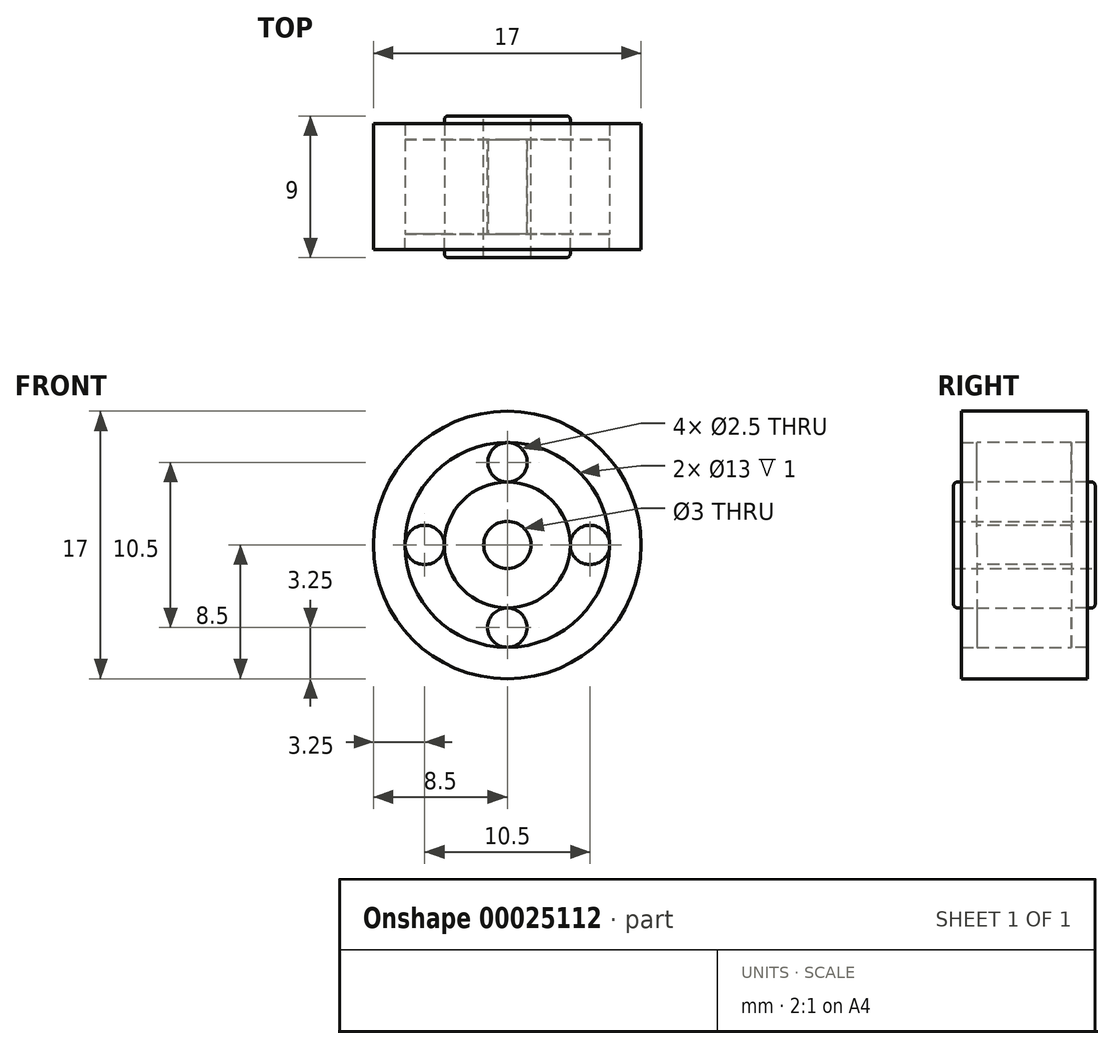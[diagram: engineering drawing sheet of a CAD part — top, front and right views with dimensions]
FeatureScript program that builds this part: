
annotation { "Feature Type Name" : "Feature", "Feature Type Description" : "" }
export const myFeature = defineFeature(function(context is Context, id is Id, definition is map)
    precondition{}
    {
        {
            var Q0;
            Q0=qCreatedBy(makeId("Front.planeOp"),FACE);
            var sketch = newSketch(context, id + "F0", { "sketchPlane" : qUnion([Q0])});
            skCircle(sketch, "E0", {"center": v(0, 0) * mm, "radius": 8.5 * mm});
            skCircle(sketch, "E1", {"center": v(0, 0) * mm, "radius": 1.5 * mm});
            skCircle(sketch, "E2", {"center": v(0, 0) * mm, "radius": 4 * mm});
            skCircle(sketch, "E3", {"center": v(0, 0) * mm, "radius": 6.5 * mm});
            skCircle(sketch, "E4", {"center": v(0, -5.25) * mm, "radius": 1.25 * mm});
            skSolve(sketch);
        }
        {
            var Q0;
            Q0 = qSketchRegion(id + "F0", true);
            var Q1;
            {var subQ3=sQuery(id+"F0.wireOp",EDGE,"E2");Q1=makeQuery(id+"F0.imprint","IMPRINT",FACE,{"disambiguationData":[TD([[makeQuery(id+"F0.imprint","IMPRINT",EDGE,{"derivedFrom":subQ3}),-1.0]])]});}
            var Q2;
            Q2=makeQuery(id+"F0.imprint","IMPRINT",FACE,{"disambiguationData":[TD([[makeQuery(id+"F0.imprint","IMPRINT",EDGE,{"derivedFrom":sQuery(id+"F0.wireOp",EDGE,"E1")}),-1.0]])]});
            extrude(context, id + "F1", {"entities" : qUnion([Q0, Q1, Q2]), "depth" : 6 * mm});
        }
        {
            var Q0;
            Q0=makeQuery(id+"F1.opExtrude","CAP_FACE",FACE,{"disambiguationData":[OSD([sQuery(id+"F0.wireOp",EDGE,"E0"),sQuery(id+"F0.wireOp",EDGE,"E1"),sQuery(id+"F0.wireOp",EDGE,"E4")])],"isStart":false});
            var sketch = newSketch(context, id + "F2", { "sketchPlane" : qUnion([Q0])});
            skCircle(sketch, "E5", {"center": v(0, 0) * mm, "radius": 4 * mm});
            skSolve(sketch);
        }
        {
            var Q0;
            Q0=makeQuery(id+"F2.imprint","IMPRINT",FACE,{"disambiguationData":[TD([[makeQuery(id+"F2.imprint","IMPRINT",EDGE,{"derivedFrom":sQuery(id+"F2.wireOp",EDGE,"E5")}),1.0]])]});
            extrude(context, id + "F3", {"entities" : qUnion([Q0]), "operationType" : NewBodyOperationType.ADD, "depth" : 1.5 * mm});
        }
        {
            var Q0;
            Q0=makeQuery(id+"F1.opExtrude","CAP_FACE",FACE,{"disambiguationData":[OSD([sQuery(id+"F0.wireOp",EDGE,"E0"),sQuery(id+"F0.wireOp",EDGE,"E1"),sQuery(id+"F0.wireOp",EDGE,"E4")])],"isStart":false});
            var sketch = newSketch(context, id + "F4", { "sketchPlane" : qUnion([Q0])});
            skCircle(sketch, "E6", {"center": v(0, 0) * mm, "radius": 6.5 * mm});
            skSolve(sketch);
        }
        {
            var Q0;
            Q0=makeQuery(id+"F4.imprint","IMPRINT",FACE,{"disambiguationData":[TD([[makeQuery(id+"F4.imprint","IMPRINT",EDGE,{"derivedFrom":sQuery(id+"F4.wireOp",EDGE,"E6")}),-1.0]])]});
            extrude(context, id + "F5", {"entities" : qUnion([Q0]), "operationType" : NewBodyOperationType.ADD, "depth" : 1 * mm});
        }
        {
            var Q0;
            Q0=makeQuery(id+"F1.opExtrude","CAP_FACE",FACE,{"disambiguationData":[OSD([sQuery(id+"F0.wireOp",EDGE,"E0"),sQuery(id+"F0.wireOp",EDGE,"E1"),sQuery(id+"F0.wireOp",EDGE,"E4")])],"isStart":false});
            var sketch = newSketch(context, id + "F6", { "sketchPlane" : qUnion([Q0])});
            skLineSegment(sketch, "E7", {"start": v(0, 0) * mm, "end": v(0, -6.5) * mm, "construction": true});
            skLineSegment(sketch, "E8", {"start": v(0, 0) * mm, "end": v(0, 6.5) * mm, "construction": true});
            skLineSegment(sketch, "E9", {"start": v(0, 0) * mm, "end": v(6.5, 0) * mm, "construction": true});
            skLineSegment(sketch, "E10", {"start": v(0, 0) * mm, "end": v(-6.5, 0) * mm, "construction": true});
            skCircle(sketch, "E11", {"center": v(5.25, 0) * mm, "radius": 1.25 * mm});
            skCircle(sketch, "E12", {"center": v(0.01, 5.25) * mm, "radius": 1.25 * mm});
            skCircle(sketch, "E13", {"center": v(-5.25, 0) * mm, "radius": 1.25 * mm});
            skSolve(sketch);
        }
        {
            var Q0;
            {var subQ0=sQuery(id+"F6.wireOp",EDGE,"E11");var subQ2=makeQuery(id+"F6.imprint","INTERSECT",VERTEX,{"derivedFrom":[makeQuery(id+"F5.opExtrude","CAP_EDGE",EDGE,{"disambiguationData":[OSD([sQuery(id+"F4.wireOp",EDGE,"E6")])],"isStart":true}),subQ0]});Q0=makeQuery(id+"F6.imprint","IMPRINT",FACE,{"disambiguationData":[TD([[makeQuery(id+"F6.imprint","IMPRINT",EDGE,{"disambiguationData":[TD([[subQ2,-1.0]])],"derivedFrom":subQ0}),1.0]])]});}
            var Q1;
            {var subQ0=sQuery(id+"F6.wireOp",EDGE,"E13");var subQ2=makeQuery(id+"F6.imprint","INTERSECT",VERTEX,{"derivedFrom":[makeQuery(id+"F5.opExtrude","CAP_EDGE",EDGE,{"disambiguationData":[OSD([sQuery(id+"F4.wireOp",EDGE,"E6")])],"isStart":true}),subQ0]});Q1=makeQuery(id+"F6.imprint","IMPRINT",FACE,{"disambiguationData":[TD([[makeQuery(id+"F6.imprint","IMPRINT",EDGE,{"disambiguationData":[TD([[subQ2,1.0]])],"derivedFrom":subQ0}),1.0]])]});}
            var Q2;
            {var subQ0=sQuery(id+"F6.wireOp",EDGE,"E12");var subQ2=makeQuery(id+"F6.imprint","INTERSECT",VERTEX,{"derivedFrom":[makeQuery(id+"F5.opExtrude","CAP_EDGE",EDGE,{"disambiguationData":[OSD([sQuery(id+"F4.wireOp",EDGE,"E6")])],"isStart":true}),subQ0]});Q2=makeQuery(id+"F6.imprint","IMPRINT",FACE,{"disambiguationData":[TD([[makeQuery(id+"F6.imprint","IMPRINT",EDGE,{"disambiguationData":[TD([[subQ2,-1.0]])],"derivedFrom":subQ0}),1.0]])]});}
            extrude(context, id + "F7", {"entities" : qUnion([Q0, Q1, Q2]), "operationType" : NewBodyOperationType.REMOVE, "oppositeDirection" : true, "depth" : 25.4 * mm});
        }
        {
            var Q0;
            Q0=makeQuery(id+"F1.opExtrude","CAP_FACE",FACE,{"disambiguationData":[OSD([sQuery(id+"F0.wireOp",EDGE,"E0"),sQuery(id+"F0.wireOp",EDGE,"E1"),sQuery(id+"F0.wireOp",EDGE,"E4")])],"isStart":true});
            var sketch = newSketch(context, id + "F8", { "sketchPlane" : qUnion([Q0])});
            skCircle(sketch, "E14", {"center": v(0, 0) * mm, "radius": 4 * mm});
            skSolve(sketch);
        }
        {
            var Q0;
            {var subQ3=sQuery(id+"F0.wireOp",EDGE,"E1");Q0=makeQuery(id+"F8.imprint","IMPRINT",FACE,{"disambiguationData":[TD([[makeQuery(id+"F8.imprint","IMPRINT",EDGE,{"derivedFrom":makeQuery(id+"F1.opExtrude","CAP_EDGE",EDGE,{"disambiguationData":[OSD([subQ3])],"isStart":true})}),1.0]])]});}
            extrude(context, id + "F9", {"entities" : qUnion([Q0]), "operationType" : NewBodyOperationType.ADD, "depth" : 1.5 * mm});
        }
        {
            var Q0;
            Q0=makeQuery(id+"F1.opExtrude","CAP_FACE",FACE,{"disambiguationData":[OSD([sQuery(id+"F0.wireOp",EDGE,"E0"),sQuery(id+"F0.wireOp",EDGE,"E1"),sQuery(id+"F0.wireOp",EDGE,"E4")])],"isStart":true});
            var sketch = newSketch(context, id + "F10", { "sketchPlane" : qUnion([Q0])});
            skCircle(sketch, "E15", {"center": v(0, 0) * mm, "radius": 6.5 * mm});
            skSolve(sketch);
        }
        {
            var Q0;
            {var subQ0=sQuery(id+"F0.wireOp",EDGE,"E0");Q0=makeQuery(id+"F10.imprint","IMPRINT",FACE,{"disambiguationData":[TD([[makeQuery(id+"F10.imprint","IMPRINT",EDGE,{"derivedFrom":makeQuery(id+"F1.opExtrude","CAP_EDGE",EDGE,{"disambiguationData":[OSD([subQ0])],"isStart":true})}),-1.0]])]});}
            extrude(context, id + "F11", {"entities" : qUnion([Q0]), "operationType" : NewBodyOperationType.ADD, "depth" : 1 * mm});
        }
        {
            var Q0;
            Q0=makeQuery(id+"F9.opExtrude","CAP_EDGE",EDGE,{"disambiguationData":[OSD([sQuery(id+"F8.wireOp",EDGE,"E14")])],"isStart":false});
            fillet(context, id + "F12", {"entities" : qUnion([Q0]), "radius" : 0.24 * mm, "tangentPropagation" : true, "allowEdgeOverflow" : false});
        }
        {
            var Q0;
            Q0=makeQuery(id+"F3.opExtrude","CAP_EDGE",EDGE,{"disambiguationData":[OSD([sQuery(id+"F2.wireOp",EDGE,"E5")])],"isStart":false});
            fillet(context, id + "F13", {"entities" : qUnion([Q0]), "radius" : 0.25 * mm, "tangentPropagation" : true, "allowEdgeOverflow" : false});
        }
    });
